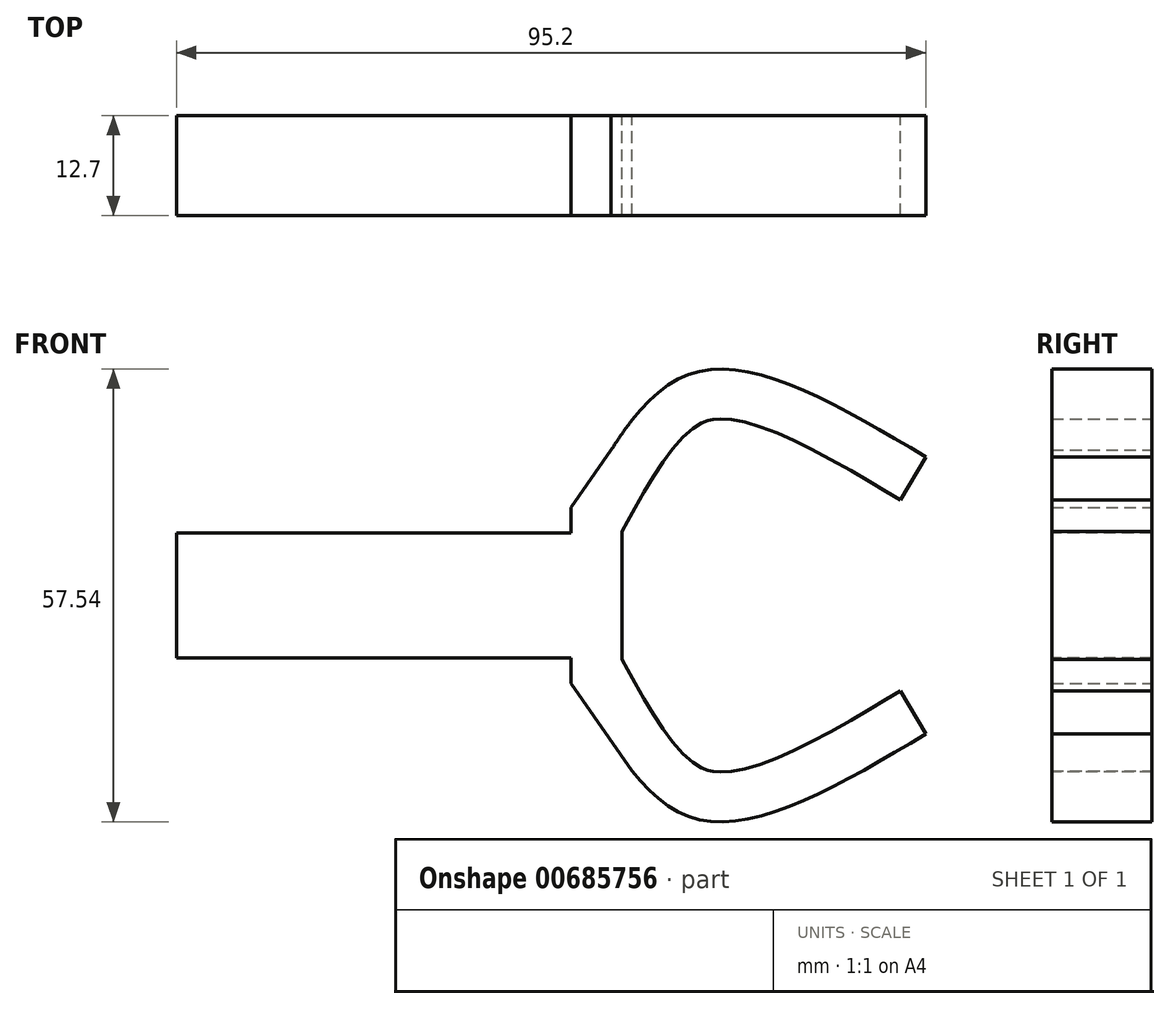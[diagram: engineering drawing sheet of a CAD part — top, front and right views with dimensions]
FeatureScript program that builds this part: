
annotation { "Feature Type Name" : "Feature", "Feature Type Description" : "" }
export const myFeature = defineFeature(function(context is Context, id is Id, definition is map)
    precondition{}
    {
        {
            var Q0;
            Q0=qCreatedBy(makeId("Right.planeOp"),FACE);
            var sketch = newSketch(context, id + "F0", { "sketchPlane" : qUnion([Q0])});
            skLineSegment(sketch, "E0.bottom", {"start": v(6.35, 7.94) * mm, "end": v(-6.35, 7.94) * mm});
            skLineSegment(sketch, "E0.top", {"start": v(6.35, -7.94) * mm, "end": v(-6.35, -7.94) * mm});
            skLineSegment(sketch, "E0.left", {"start": v(6.35, 7.94) * mm, "end": v(6.35, -7.94) * mm});
            skLineSegment(sketch, "E0.right", {"start": v(-6.35, 7.94) * mm, "end": v(-6.35, -7.94) * mm});
            skPoint(sketch, "E0.middle", {"position": v(0, 0) * mm});
            skSolve(sketch);
        }
        {
            var Q0;
            Q0=makeQuery(id+"F0.imprint","IMPRINT",FACE,{"disambiguationData":[TD([[makeQuery(id+"F0.imprint","IMPRINT",EDGE,{"derivedFrom":sQuery(id+"F0.wireOp",EDGE,"E0.bottom")}),1.0]])]});
            extrude(context, id + "F1", {"entities" : qUnion([Q0]), "depth" : 25.4 * mm});
        }
        {
            var Q0;
            Q0=qCreatedBy(makeId("Front.planeOp"),FACE);
            var sketch = newSketch(context, id + "F2", { "sketchPlane" : qUnion([Q0])});
            skFitSpline(sketch, "E1", {"points": [v(25.63, 11.2) * mm, v(40.76, 28.42) * mm, v(69.8, 17.6) * mm], "startDerivative": vector(27.8, 50.52) * mm, "endDerivative": vector(59.74, -35.57) * mm});
            skFitSpline(sketch, "E2.MirrorCS", {"points": [v(25.63, -11.2) * mm, v(40.76, -28.42) * mm, v(69.8, -17.6) * mm], "startDerivative": vector(27.8, -50.52) * mm, "endDerivative": vector(59.74, 35.57) * mm});
            skFitSpline(sketch, "E3.0", {"points": [v(31.2, 8.13) * mm, v(31.77, 9.19) * mm, v(32.91, 11.25) * mm, v(34.58, 14.15) * mm, v(36.23, 16.73) * mm, v(37.85, 18.9) * mm, v(39.39, 20.55) * mm, v(40.54, 21.45) * mm, v(41.34, 21.9) * mm, v(41.8, 22.1) * mm, v(42.16, 22.22) * mm, v(42.42, 22.3) * mm, v(42.7, 22.35) * mm, v(43.14, 22.4) * mm, v(43.76, 22.43) * mm, v(44.96, 22.37) * mm, v(46.8, 22.04) * mm, v(49.48, 21.2) * mm, v(52.5, 19.93) * mm, v(55.77, 18.32) * mm, v(60.4, 15.8) * mm, v(64.06, 13.62) * mm, v(66.55, 12.14) * mm]});
            skFitSpline(sketch, "E4.0", {"points": [v(31.2, -8.13) * mm, v(31.77, -9.19) * mm, v(32.91, -11.25) * mm, v(34.58, -14.15) * mm, v(36.23, -16.73) * mm, v(37.85, -18.9) * mm, v(39.39, -20.55) * mm, v(40.54, -21.45) * mm, v(41.34, -21.9) * mm, v(41.8, -22.1) * mm, v(42.16, -22.22) * mm, v(42.42, -22.3) * mm, v(42.7, -22.35) * mm, v(43.14, -22.4) * mm, v(43.76, -22.43) * mm, v(44.96, -22.37) * mm, v(46.8, -22.04) * mm, v(49.48, -21.2) * mm, v(52.5, -19.93) * mm, v(55.77, -18.32) * mm, v(60.4, -15.8) * mm, v(64.06, -13.62) * mm, v(66.55, -12.14) * mm]});
            skLineSegment(sketch, "E5", {"start": v(31.2, 8.13) * mm, "end": v(31.2, -8.13) * mm});
            skLineSegment(sketch, "E6", {"start": v(69.8, 17.6) * mm, "end": v(66.55, 12.14) * mm});
            skLineSegment(sketch, "E7", {"start": v(66.55, -12.14) * mm, "end": v(69.8, -17.6) * mm});
            skLineSegment(sketch, "E8", {"start": v(25.63, 11.2) * mm, "end": v(24.74, 11.2) * mm});
            skLineSegment(sketch, "E9", {"start": v(24.74, 11.2) * mm, "end": v(24.74, -11.1) * mm});
            skLineSegment(sketch, "E10", {"start": v(24.74, -11.1) * mm, "end": v(25.63, -11.2) * mm});
            skLineSegment(sketch, "E11", {"start": v(24.74, 11.2) * mm, "end": v(32.48, 22.29) * mm});
            skLineSegment(sketch, "E12.MirrorCS", {"start": v(24.74, -11.2) * mm, "end": v(32.48, -22.29) * mm});
            skLineSegment(sketch, "E13", {"start": v(24.74, -11.1) * mm, "end": v(24.74, -11.2) * mm});
            skSolve(sketch);
        }
        {
            var Q0;
            Q0=makeQuery(id+"F2.imprint","IMPRINT",FACE,{"disambiguationData":[TD([[makeQuery(id+"F2.imprint","IMPRINT",EDGE,{"derivedFrom":sQuery(id+"F2.wireOp",EDGE,"E1")}),-1.0]])]});
            var Q1;
            Q1=makeQuery(id+"F2.imprint","IMPRINT",FACE,{"disambiguationData":[TD([[makeQuery(id+"F2.imprint","IMPRINT",EDGE,{"derivedFrom":sQuery(id+"F2.wireOp",EDGE,"E3.0")}),1.0]])]});
            var Q2;
            {var subQ0=sQuery(id+"F2.wireOp",EDGE,"E10");Q2=makeQuery(id+"F2.imprint","IMPRINT",FACE,{"disambiguationData":[TD([[makeQuery(id+"F2.imprint","IMPRINT",EDGE,{"derivedFrom":subQ0}),-1.0]])]});}
            var Q3;
            {var subQ0=sQuery(id+"F2.wireOp",EDGE,"E8");Q3=makeQuery(id+"F2.imprint","IMPRINT",FACE,{"disambiguationData":[TD([[makeQuery(id+"F2.imprint","IMPRINT",EDGE,{"derivedFrom":subQ0}),-1.0]])]});}
            extrude(context, id + "F3", {"entities" : qUnion([Q0, Q1, Q2, Q3]), "operationType" : NewBodyOperationType.ADD, "endBound" : BoundingType.SYMMETRIC, "depth" : 12.7 * mm});
        }
        {
            var Q0;
            Q0=makeQuery(id+"F1.opExtrude","CAP_FACE",FACE,{"disambiguationData":[OSD([sQuery(id+"F0.wireOp",EDGE,"E0.bottom"),sQuery(id+"F0.wireOp",EDGE,"E0.top"),sQuery(id+"F0.wireOp",EDGE,"E0.left"),sQuery(id+"F0.wireOp",EDGE,"E0.right")])],"isStart":true});
            var sketch = newSketch(context, id + "F4", { "sketchPlane" : qUnion([Q0])});
            skPoint(sketch, "E14", {"position": v(0, 1.59) * mm});
            skCircle(sketch, "E15", {"center": v(0, 1.59) * mm, "radius": 3.18 * mm});
            skSolve(sketch);
        }
        {
            var Q0;
            Q0=makeQuery(id+"F4.imprint","IMPRINT",FACE,{"disambiguationData":[TD([[makeQuery(id+"F4.imprint","IMPRINT",EDGE,{"derivedFrom":sQuery(id+"F4.wireOp",EDGE,"E15")}),1.0]])]});
            extrude(context, id + "F5", {"entities" : qUnion([Q0]), "oppositeDirection" : true, "depth" : 25.4 * mm});
        }
        {
            var Q0;
            Q0=makeQuery(id+"F1.opExtrude","CAP_FACE",FACE,{"disambiguationData":[OSD([sQuery(id+"F0.wireOp",EDGE,"E0.bottom"),sQuery(id+"F0.wireOp",EDGE,"E0.top"),sQuery(id+"F0.wireOp",EDGE,"E0.left"),sQuery(id+"F0.wireOp",EDGE,"E0.right")])],"isStart":true});
            extrude(context, id + "F6", {"entities" : qUnion([Q0]), "operationType" : NewBodyOperationType.ADD, "depth" : 25.4 * mm});
        }
    });
